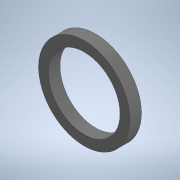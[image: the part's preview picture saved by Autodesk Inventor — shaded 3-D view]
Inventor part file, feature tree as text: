
AUTODESK INVENTOR PART (.ipt)
format: ipt  version: 2020 (Build 240168000, 168)  size: 101,888 bytes
history: native  units: mm
features: extrude x1, sketch x1
ambient origin geometry x8: Origin, YZ Plane, XZ Plane, XY Plane, X Axis, Y Axis, Z Axis, Center Point
bodies: Solid1 (feature_tree)
feature tree (2):
  extrude  "Extrusion1"  Depth=4.0mm
  sketch  "Sketch1"  dims[d0=25.0mm d1=32.0mm d2=4.0mm d3=0.0mm]
